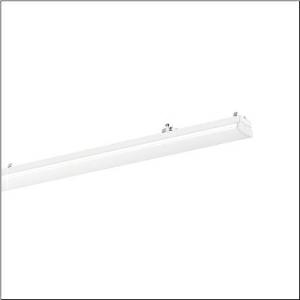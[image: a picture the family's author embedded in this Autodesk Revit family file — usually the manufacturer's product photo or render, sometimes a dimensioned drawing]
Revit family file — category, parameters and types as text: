
# Revit family: licross_r__21_recessed_opal_mo_52te1ddn445g_24f8
name_source: partatom
category: Lighting Fixtures
units: mm (PartAtom-declared; Revit-internal decimal feet)

## family parameters
Cut with Voids When Loaded = No
Host = Face
Light Source = No
Part Type = Normal
Room Calculation Point = No
Round Connector Dimension = Use Diameter
Shared = No

## types (1)
- --- (1 x LED, 4500 lm, 25.8 W, 4000K)
    Apparent Load = 26 VA
    CIE Flux Codes = 44 73 91 87 100
    Color Rendering = 80
    Color Temperature = 4000K
    Default Elevation = 1800 mm
    Description = Licross® 21 recessed opal MO, luminaire insert, of sheet steel, galvanised, coil coated, white, length: 1.500mm, width: 66mm, height: 67mm, LED rated luminous flux: 4.500lm, light colour: 840, control gear: DALI 2, with plug, 5-pole, with phase selection, mains connection: 220..240V, AC, 50/60Hz, rated input power: 26W, internal wiring halogen-free, primary optical cover: cover, of PMMA, light emission: direct with ceiling illumination distribution, primary light characteristic: symmetric, protection rating (complete): IP54, insulation class (complete): insulation class I (protective earthing), certification: CE, ENEC, VDE, UKCA, protection symbol: D if used in an environment with non-conductive dust loads with corresponding accessories, impact resistance: IK06, permissible ambient temperature for indoor applications: -25..+45°C, corresponds to IFS (International Featured Standards) requirements for safety and quality in the food industry, reducing of maximum allowable ambient temperature of 5°C with ceiling mounting, LABS conformity tested according to VDMA 24364:2018-05, packaging unit: 1 piece
    Height = 83 mm
    Lamp = 1 x LED
    Lamp Light Flux = 4500 lm
    Lamp Power = 25.8 W
    Lamp count = 1
    Length = 1500 mm
    Luminous efficacy = 174 lm/W
    Manufacturer = Siteco
    ModVariant = No
    Model = 52TE1DDN445G
    Mounting Place = Ceiling
    Mounting Type = Pendant
    Number of Poles = 1
    OnlyDefault = Yes
    Power Factor = 1
    Product Name = Licross® 21 recessed opal MO
    Product group = luminaire insert | ceiling pendant
    ProductGroupID = 902
    Protection Class = Protection class I
    Protection Degree = IP 54
    RLX_Detail_Level = 1
    RLX_Emergency_Light_Flux = 0 lm
    RLX_Emergency_Type = 0
    RLX_Emergency_Type_DB = No
    RlxData = <blob elided: 26517 chars, md5=cb917706>
    Socket = socket
    Standby Power = 0 W
    System Light Flux = 4500 lm
    System Power = 26 W
    Type Comments = factory setting: luminous flux: 100 % | dim-lin: 254 | 172 mA
    Type Image = l_1313666.jpg
    URL = http://relux.com
    VarID = @adj_084489
    Voltage = 0 V
    Weight = 0.00 kg
    Width = 76 mm

## geometry (parser evidence)
native form markers: Blend x4, Sweep x13
no freeform markers — native parametric forms only
